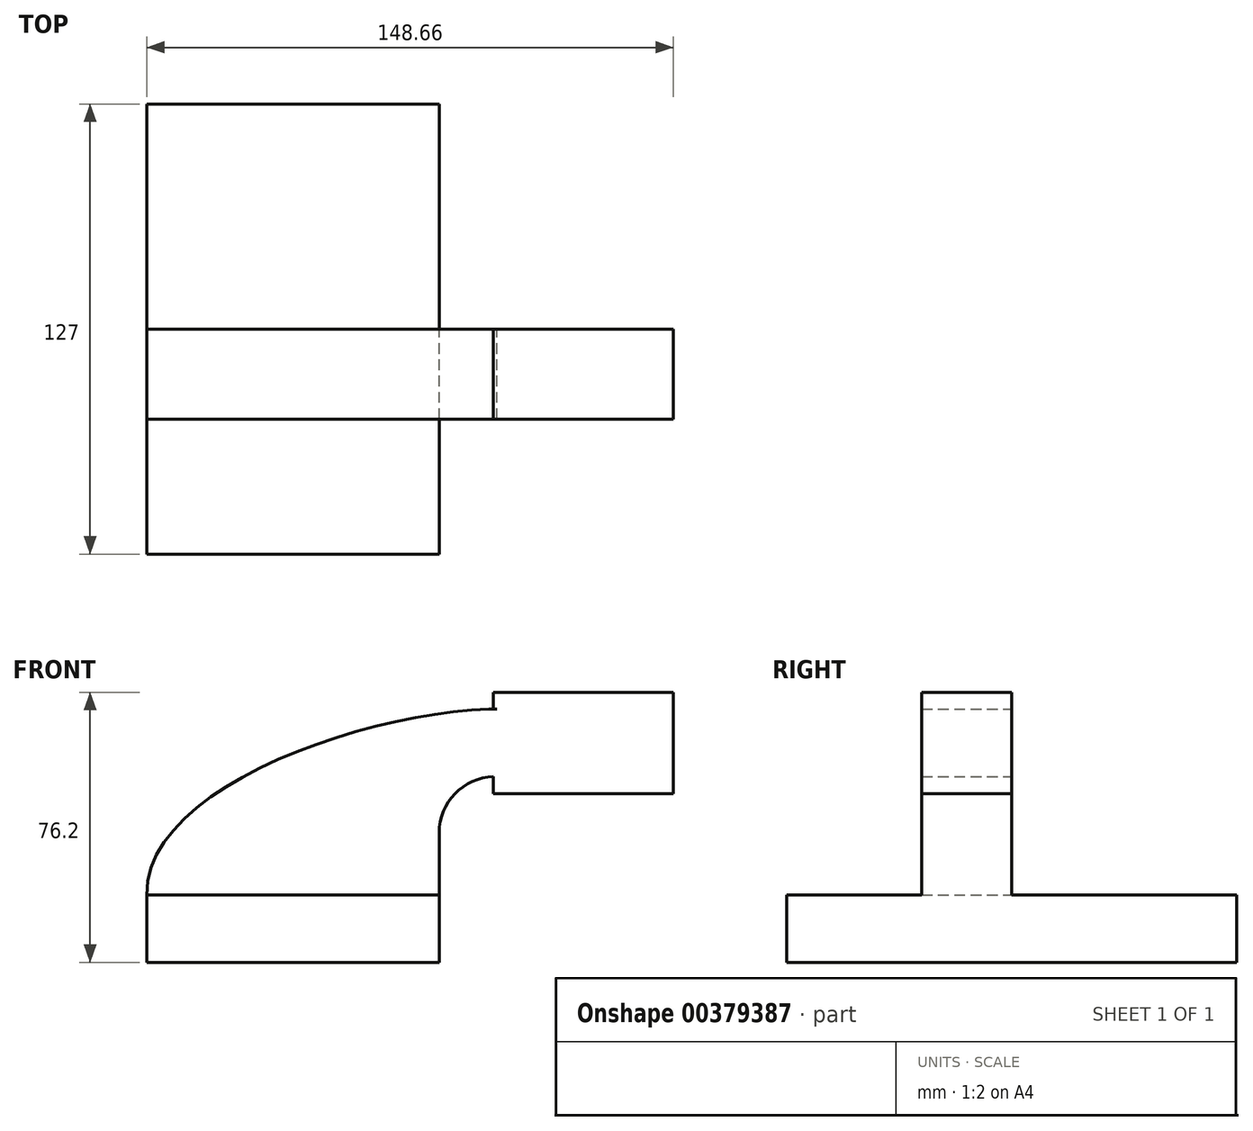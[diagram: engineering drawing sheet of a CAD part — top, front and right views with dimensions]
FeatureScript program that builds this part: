
annotation { "Feature Type Name" : "Feature", "Feature Type Description" : "" }
export const myFeature = defineFeature(function(context is Context, id is Id, definition is map)
    precondition{}
    {
        {
            var Q0;
            Q0=qCreatedBy(makeId("Front.planeOp"),FACE);
            var sketch = newSketch(context, id + "F0", { "sketchPlane" : qUnion([Q0])});
            skLineSegment(sketch, "E0.bottom", {"start": v(-72.04, -11.72) * mm, "end": v(10.51, -11.72) * mm});
            skLineSegment(sketch, "E0.top", {"start": v(-72.04, -30.77) * mm, "end": v(10.51, -30.77) * mm});
            skLineSegment(sketch, "E0.left", {"start": v(-72.04, -11.72) * mm, "end": v(-72.04, -30.77) * mm});
            skLineSegment(sketch, "E0.right", {"start": v(10.51, -11.72) * mm, "end": v(10.51, -30.77) * mm});
            skLineSegment(sketch, "E1.bottom", {"start": v(25.82, 45.43) * mm, "end": v(76.62, 45.43) * mm});
            skLineSegment(sketch, "E1.top", {"start": v(25.82, 16.86) * mm, "end": v(76.62, 16.86) * mm});
            skLineSegment(sketch, "E1.left", {"start": v(25.82, 45.43) * mm, "end": v(25.82, 16.86) * mm});
            skLineSegment(sketch, "E1.right", {"start": v(76.62, 45.43) * mm, "end": v(76.62, 16.86) * mm});
            skLineSegment(sketch, "E2", {"start": v(10.51, -11.72) * mm, "end": v(10.51, 5.76) * mm});
            skArc(sketch, "E3", {"start": v(10.51, 5.76) * mm, "mid": v(15.25, 17.07) * mm, "end": v(26.63, 21.63) * mm});
            skLineSegment(sketch, "E4", {"start": v(26.63, 21.63) * mm, "end": v(56.05, 21.63) * mm});
            skLineSegment(sketch, "E5.0", {"start": v(26.75, 40.68) * mm, "end": v(56.05, 40.68) * mm});
            skArc(sketch, "E5.1", {"start": v(-8.54, 5.76) * mm, "mid": v(1.82, 30.58) * mm, "end": v(26.75, 40.68) * mm});
            skLineSegment(sketch, "E5.2", {"start": v(-8.54, -10.63) * mm, "end": v(-8.54, 5.76) * mm});
            skFitSpline(sketch, "E6", {"points": [v(26.75, 40.68) * mm, v(-72.04, -11.72) * mm], "startDerivative": vector(-108.37, -1.1) * mm, "endDerivative": vector(1.37, -91.52) * mm});
            skSolve(sketch);
        }
        {
            var Q0;
            Q0=makeQuery(id+"F0.imprint","IMPRINT",FACE,{"disambiguationData":[TD([[makeQuery(id+"F0.imprint","IMPRINT",EDGE,{"derivedFrom":sQuery(id+"F0.wireOp",EDGE,"E0.bottom")}),-1.0]])]});
            extrude(context, id + "F1", {"entities" : qUnion([Q0]), "endBound" : BoundingType.SYMMETRIC, "depth" : 127 * mm});
        }
        {
            var Q0;
            {var subQ4=sQuery(id+"F0.wireOp",EDGE,"E0.bottom");Q0=makeQuery(id+"F0.imprint","IMPRINT",FACE,{"disambiguationData":[TD([[makeQuery(id+"F0.imprint","IMPRINT",EDGE,{"derivedFrom":subQ4}),1.0]])]});}
            var Q1;
            {var subQ4=sQuery(id+"F0.wireOp",EDGE,"E1.bottom");Q1=makeQuery(id+"F0.imprint","IMPRINT",FACE,{"disambiguationData":[TD([[makeQuery(id+"F0.imprint","IMPRINT",EDGE,{"derivedFrom":subQ4}),-1.0]])]});}
            extrude(context, id + "F2", {"entities" : qUnion([Q0, Q1]), "operationType" : NewBodyOperationType.ADD, "depth" : 25.4 * mm});
        }
    });
